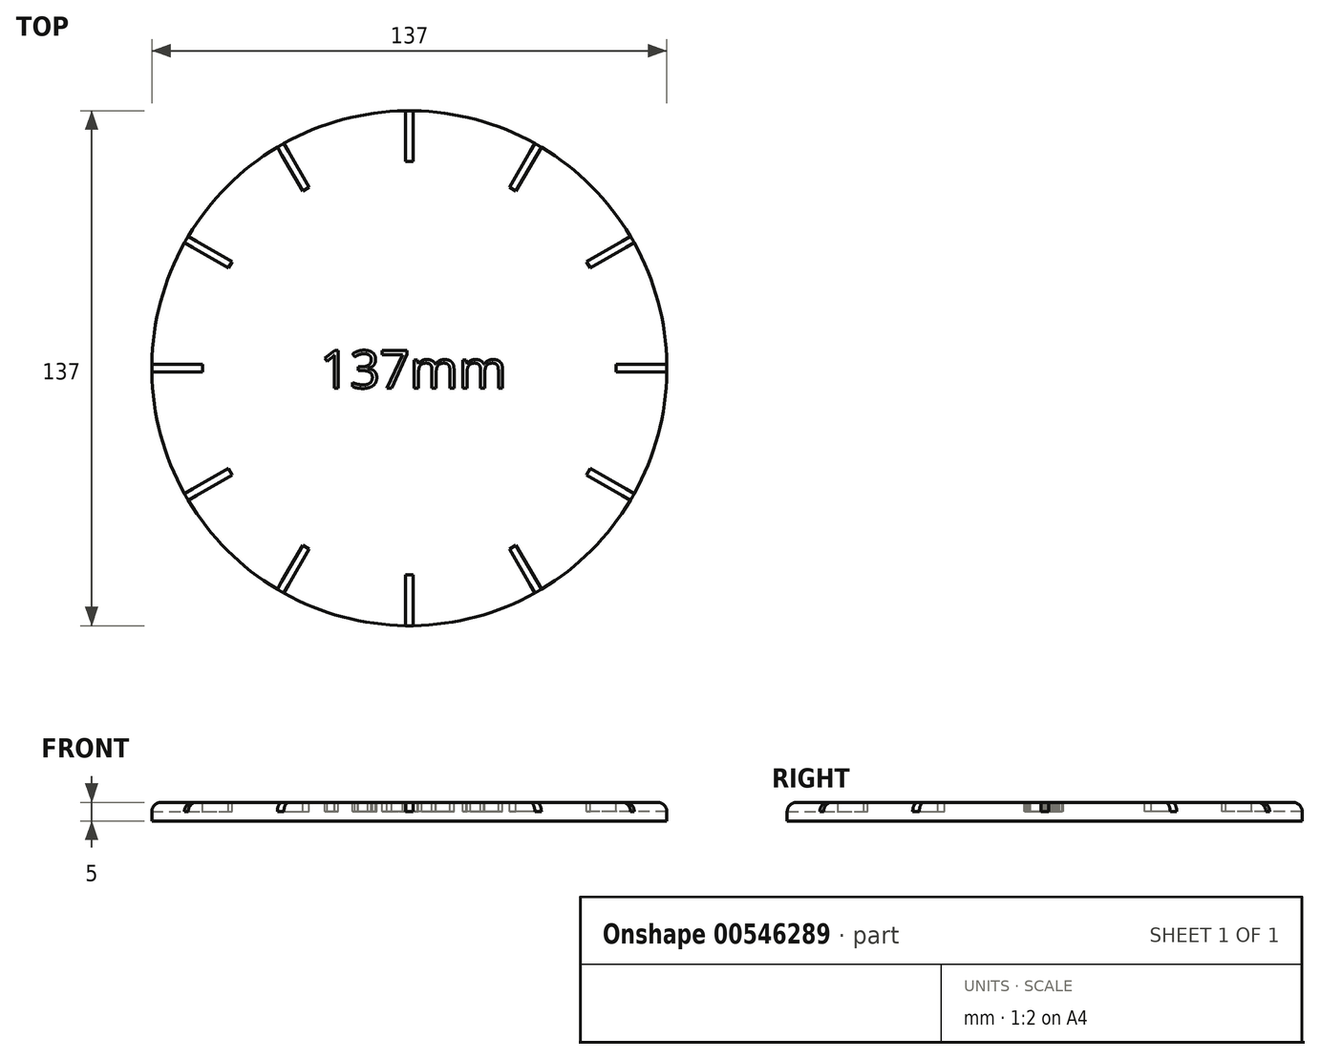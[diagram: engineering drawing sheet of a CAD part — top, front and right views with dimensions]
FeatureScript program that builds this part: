
annotation { "Feature Type Name" : "Feature", "Feature Type Description" : "" }
export const myFeature = defineFeature(function(context is Context, id is Id, definition is map)
    precondition{}
    {
        {
            var Q0;
            Q0=qCreatedBy(makeId("Top.planeOp"),FACE);
            var sketch = newSketch(context, id + "F0", { "sketchPlane" : qUnion([Q0])});
            skCircle(sketch, "E0", {"center": v(0, 0) * mm, "radius": 68.5 * mm});
            skSolve(sketch);
        }
        {
            var Q0;
            Q0=qSketchRegion(id+"F0",true);
            extrude(context, id + "F1", {"entities" : qUnion([Q0]), "depth" : 5 * mm, "offsetDistance" : 25 * mm});
        }
        {
            var Q0;
            Q0=makeQuery(id+"F1.opExtrude","CAP_FACE",FACE,{"disambiguationData":[OSD([sQuery(id+"F0.wireOp",EDGE,"E0")])],"isStart":false});
            var sketch = newSketch(context, id + "F2", { "sketchPlane" : qUnion([Q0])});
            skLineSegment(sketch, "E1.bottom", {"start": v(-1, 70) * mm, "end": v(1, 70) * mm});
            skLineSegment(sketch, "E1.top", {"start": v(-1, 55) * mm, "end": v(1, 55) * mm});
            skLineSegment(sketch, "E1.left", {"start": v(-1, 70) * mm, "end": v(-1, 55) * mm});
            skLineSegment(sketch, "E1.right", {"start": v(1, 70) * mm, "end": v(1, 55) * mm});
            skLineSegment(sketch, "E2.1.0", {"start": v(-35.87, 60.12) * mm, "end": v(-28.37, 47.13) * mm});
            skLineSegment(sketch, "E2.1.1", {"start": v(-34.13, 61.12) * mm, "end": v(-26.63, 48.13) * mm});
            skLineSegment(sketch, "E2.1.2", {"start": v(-28.37, 47.13) * mm, "end": v(-26.63, 48.13) * mm});
            skLineSegment(sketch, "E2.1.3", {"start": v(-35.87, 60.12) * mm, "end": v(-34.13, 61.12) * mm});
            skLineSegment(sketch, "E2.2.0", {"start": v(-61.12, 34.13) * mm, "end": v(-48.13, 26.63) * mm});
            skLineSegment(sketch, "E2.2.1", {"start": v(-60.12, 35.87) * mm, "end": v(-47.13, 28.37) * mm});
            skLineSegment(sketch, "E2.2.2", {"start": v(-48.13, 26.63) * mm, "end": v(-47.13, 28.37) * mm});
            skLineSegment(sketch, "E2.2.3", {"start": v(-61.12, 34.13) * mm, "end": v(-60.12, 35.87) * mm});
            skPoint(sketch, "E2.center", {"position": v(0, 0) * mm});
            skLineSegment(sketch, "E3.2.3.0", {"start": v(-70, -1) * mm, "end": v(-55, -1) * mm});
            skLineSegment(sketch, "E3.3.3.0", {"start": v(-70, 1) * mm, "end": v(-55, 1) * mm});
            skLineSegment(sketch, "E3.6.3.0", {"start": v(-55, -1) * mm, "end": v(-55, 1) * mm});
            skLineSegment(sketch, "E3.9.3.0", {"start": v(-70, -1) * mm, "end": v(-70, 1) * mm});
            skLineSegment(sketch, "E3.2.4.0", {"start": v(-60.12, -35.87) * mm, "end": v(-47.13, -28.37) * mm});
            skLineSegment(sketch, "E3.3.4.0", {"start": v(-61.12, -34.13) * mm, "end": v(-48.13, -26.63) * mm});
            skLineSegment(sketch, "E3.6.4.0", {"start": v(-47.13, -28.37) * mm, "end": v(-48.13, -26.63) * mm});
            skLineSegment(sketch, "E3.9.4.0", {"start": v(-60.12, -35.87) * mm, "end": v(-61.12, -34.13) * mm});
            skLineSegment(sketch, "E3.2.5.0", {"start": v(-34.13, -61.12) * mm, "end": v(-26.63, -48.13) * mm});
            skLineSegment(sketch, "E3.3.5.0", {"start": v(-35.87, -60.12) * mm, "end": v(-28.37, -47.13) * mm});
            skLineSegment(sketch, "E3.6.5.0", {"start": v(-26.63, -48.13) * mm, "end": v(-28.37, -47.13) * mm});
            skLineSegment(sketch, "E3.9.5.0", {"start": v(-34.13, -61.12) * mm, "end": v(-35.87, -60.12) * mm});
            skLineSegment(sketch, "E3.2.6.0", {"start": v(1, -70) * mm, "end": v(1, -55) * mm});
            skLineSegment(sketch, "E3.3.6.0", {"start": v(-1, -70) * mm, "end": v(-1, -55) * mm});
            skLineSegment(sketch, "E3.6.6.0", {"start": v(1, -55) * mm, "end": v(-1, -55) * mm});
            skLineSegment(sketch, "E3.9.6.0", {"start": v(1, -70) * mm, "end": v(-1, -70) * mm});
            skLineSegment(sketch, "E3.2.7.0", {"start": v(35.87, -60.12) * mm, "end": v(28.37, -47.13) * mm});
            skLineSegment(sketch, "E3.3.7.0", {"start": v(34.13, -61.12) * mm, "end": v(26.63, -48.13) * mm});
            skLineSegment(sketch, "E3.6.7.0", {"start": v(28.37, -47.13) * mm, "end": v(26.63, -48.13) * mm});
            skLineSegment(sketch, "E3.9.7.0", {"start": v(35.87, -60.12) * mm, "end": v(34.13, -61.12) * mm});
            skLineSegment(sketch, "E3.2.8.0", {"start": v(61.12, -34.13) * mm, "end": v(48.13, -26.63) * mm});
            skLineSegment(sketch, "E3.3.8.0", {"start": v(60.12, -35.87) * mm, "end": v(47.13, -28.37) * mm});
            skLineSegment(sketch, "E3.6.8.0", {"start": v(48.13, -26.63) * mm, "end": v(47.13, -28.37) * mm});
            skLineSegment(sketch, "E3.9.8.0", {"start": v(61.12, -34.13) * mm, "end": v(60.12, -35.87) * mm});
            skLineSegment(sketch, "E3.2.9.0", {"start": v(70, 1) * mm, "end": v(55, 1) * mm});
            skLineSegment(sketch, "E3.3.9.0", {"start": v(70, -1) * mm, "end": v(55, -1) * mm});
            skLineSegment(sketch, "E3.6.9.0", {"start": v(55, 1) * mm, "end": v(55, -1) * mm});
            skLineSegment(sketch, "E3.9.9.0", {"start": v(70, 1) * mm, "end": v(70, -1) * mm});
            skLineSegment(sketch, "E3.2.10.0", {"start": v(60.12, 35.87) * mm, "end": v(47.13, 28.37) * mm});
            skLineSegment(sketch, "E3.3.10.0", {"start": v(61.12, 34.13) * mm, "end": v(48.13, 26.63) * mm});
            skLineSegment(sketch, "E3.6.10.0", {"start": v(47.13, 28.37) * mm, "end": v(48.13, 26.63) * mm});
            skLineSegment(sketch, "E3.9.10.0", {"start": v(60.12, 35.87) * mm, "end": v(61.12, 34.13) * mm});
            skLineSegment(sketch, "E3.2.11.0", {"start": v(34.13, 61.12) * mm, "end": v(26.63, 48.13) * mm});
            skLineSegment(sketch, "E3.3.11.0", {"start": v(35.87, 60.12) * mm, "end": v(28.37, 47.13) * mm});
            skLineSegment(sketch, "E3.6.11.0", {"start": v(26.63, 48.13) * mm, "end": v(28.37, 47.13) * mm});
            skLineSegment(sketch, "E3.9.11.0", {"start": v(34.13, 61.12) * mm, "end": v(35.87, 60.12) * mm});
            skSolve(sketch);
        }
        {
            var Q0;
            Q0=qSketchRegion(id+"F2",true);
            extrude(context, id + "F3", {"entities" : qUnion([Q0]), "operationType" : NewBodyOperationType.REMOVE, "oppositeDirection" : true, "depth" : 2.5 * mm, "offsetDistance" : 25 * mm});
        }
        {
            var Q0;
            Q0=makeQuery(id+"F1.opExtrude","CAP_FACE",FACE,{"disambiguationData":[OSD([sQuery(id+"F0.wireOp",EDGE,"E0")])],"isStart":false});
            var sketch = newSketch(context, id + "F4", { "sketchPlane" : qUnion([Q0])});
            skText(sketch, "E4", { "text": "137mm\n", "fontName": "OpenSans-Regular.ttf"});
            const initialGuessF4  = {"E4": [-0.02373, -0.00525, 1, 0, 0.01]};
            skSetInitialGuess(sketch, initialGuessF4);
            skSolve(sketch);
        }
        {
            var Q0;
            Q0=qSketchRegion(id+"F4",true);
            extrude(context, id + "F5", {"entities" : qUnion([Q0]), "operationType" : NewBodyOperationType.REMOVE, "oppositeDirection" : true, "depth" : 2.5 * mm, "offsetDistance" : 25 * mm});
        }
        {
            var Q0;
            {var subQ0=sQuery(id+"F0.wireOp",EDGE,"E0");Q0=makeQuery(id+"F3.boolean.opBoolean","SPLIT",EDGE,{"disambiguationData":[TD([makeQuery(id+"F3.opExtrude","SWEPT_FACE",FACE,{"disambiguationData":[OSD([sQuery(id+"F2.wireOp",EDGE,"E3.2.10.0")])]})])],"derivedFrom":makeQuery(id+"F1.opExtrude","CAP_EDGE",EDGE,{"disambiguationData":[OSD([subQ0])],"isStart":false})});}
            var Q1;
            {var subQ0=sQuery(id+"F0.wireOp",EDGE,"E0");Q1=makeQuery(id+"F3.boolean.opBoolean","SPLIT",EDGE,{"disambiguationData":[TD([makeQuery(id+"F3.opExtrude","SWEPT_FACE",FACE,{"disambiguationData":[OSD([sQuery(id+"F2.wireOp",EDGE,"E3.2.9.0")])]})])],"derivedFrom":makeQuery(id+"F1.opExtrude","CAP_EDGE",EDGE,{"disambiguationData":[OSD([subQ0])],"isStart":false})});}
            var Q2;
            {var subQ0=sQuery(id+"F0.wireOp",EDGE,"E0");Q2=makeQuery(id+"F3.boolean.opBoolean","SPLIT",EDGE,{"disambiguationData":[TD([makeQuery(id+"F3.opExtrude","SWEPT_FACE",FACE,{"disambiguationData":[OSD([sQuery(id+"F2.wireOp",EDGE,"E3.2.8.0")])]})])],"derivedFrom":makeQuery(id+"F1.opExtrude","CAP_EDGE",EDGE,{"disambiguationData":[OSD([subQ0])],"isStart":false})});}
            var Q3;
            {var subQ0=sQuery(id+"F0.wireOp",EDGE,"E0");Q3=makeQuery(id+"F3.boolean.opBoolean","SPLIT",EDGE,{"disambiguationData":[TD([makeQuery(id+"F3.opExtrude","SWEPT_FACE",FACE,{"disambiguationData":[OSD([sQuery(id+"F2.wireOp",EDGE,"E3.2.7.0")])]})])],"derivedFrom":makeQuery(id+"F1.opExtrude","CAP_EDGE",EDGE,{"disambiguationData":[OSD([subQ0])],"isStart":false})});}
            var Q4;
            {var subQ0=sQuery(id+"F0.wireOp",EDGE,"E0");Q4=makeQuery(id+"F3.boolean.opBoolean","SPLIT",EDGE,{"disambiguationData":[TD([makeQuery(id+"F3.opExtrude","SWEPT_FACE",FACE,{"disambiguationData":[OSD([sQuery(id+"F2.wireOp",EDGE,"E3.2.6.0")])]})])],"derivedFrom":makeQuery(id+"F1.opExtrude","CAP_EDGE",EDGE,{"disambiguationData":[OSD([subQ0])],"isStart":false})});}
            var Q5;
            {var subQ0=sQuery(id+"F0.wireOp",EDGE,"E0");Q5=makeQuery(id+"F3.boolean.opBoolean","SPLIT",EDGE,{"disambiguationData":[TD([makeQuery(id+"F3.opExtrude","SWEPT_FACE",FACE,{"disambiguationData":[OSD([sQuery(id+"F2.wireOp",EDGE,"E3.2.5.0")])]})])],"derivedFrom":makeQuery(id+"F1.opExtrude","CAP_EDGE",EDGE,{"disambiguationData":[OSD([subQ0])],"isStart":false})});}
            var Q6;
            {var subQ0=sQuery(id+"F0.wireOp",EDGE,"E0");Q6=makeQuery(id+"F3.boolean.opBoolean","SPLIT",EDGE,{"disambiguationData":[TD([makeQuery(id+"F3.opExtrude","SWEPT_FACE",FACE,{"disambiguationData":[OSD([sQuery(id+"F2.wireOp",EDGE,"E3.2.4.0")])]})])],"derivedFrom":makeQuery(id+"F1.opExtrude","CAP_EDGE",EDGE,{"disambiguationData":[OSD([subQ0])],"isStart":false})});}
            var Q7;
            {var subQ0=sQuery(id+"F0.wireOp",EDGE,"E0");Q7=makeQuery(id+"F3.boolean.opBoolean","SPLIT",EDGE,{"disambiguationData":[TD([makeQuery(id+"F3.opExtrude","SWEPT_FACE",FACE,{"disambiguationData":[OSD([sQuery(id+"F2.wireOp",EDGE,"E3.2.3.0")])]})])],"derivedFrom":makeQuery(id+"F1.opExtrude","CAP_EDGE",EDGE,{"disambiguationData":[OSD([subQ0])],"isStart":false})});}
            var Q8;
            {var subQ0=sQuery(id+"F0.wireOp",EDGE,"E0");Q8=makeQuery(id+"F3.boolean.opBoolean","SPLIT",EDGE,{"disambiguationData":[TD([makeQuery(id+"F3.opExtrude","SWEPT_FACE",FACE,{"disambiguationData":[OSD([sQuery(id+"F2.wireOp",EDGE,"E2.2.0")])]})])],"derivedFrom":makeQuery(id+"F1.opExtrude","CAP_EDGE",EDGE,{"disambiguationData":[OSD([subQ0])],"isStart":false})});}
            var Q9;
            {var subQ0=sQuery(id+"F0.wireOp",EDGE,"E0");Q9=makeQuery(id+"F3.boolean.opBoolean","SPLIT",EDGE,{"disambiguationData":[TD([makeQuery(id+"F3.opExtrude","SWEPT_FACE",FACE,{"disambiguationData":[OSD([sQuery(id+"F2.wireOp",EDGE,"E2.1.0")])]})])],"derivedFrom":makeQuery(id+"F1.opExtrude","CAP_EDGE",EDGE,{"disambiguationData":[OSD([subQ0])],"isStart":false})});}
            var Q10;
            {var subQ0=sQuery(id+"F0.wireOp",EDGE,"E0");Q10=makeQuery(id+"F3.boolean.opBoolean","SPLIT",EDGE,{"disambiguationData":[TD([makeQuery(id+"F3.opExtrude","SWEPT_FACE",FACE,{"disambiguationData":[OSD([sQuery(id+"F2.wireOp",EDGE,"E1.left")])]})])],"derivedFrom":makeQuery(id+"F1.opExtrude","CAP_EDGE",EDGE,{"disambiguationData":[OSD([subQ0])],"isStart":false})});}
            var Q11;
            {var subQ0=sQuery(id+"F0.wireOp",EDGE,"E0");Q11=makeQuery(id+"F3.boolean.opBoolean","SPLIT",EDGE,{"disambiguationData":[TD([makeQuery(id+"F3.opExtrude","SWEPT_FACE",FACE,{"disambiguationData":[OSD([sQuery(id+"F2.wireOp",EDGE,"E1.right")])]})])],"derivedFrom":makeQuery(id+"F1.opExtrude","CAP_EDGE",EDGE,{"disambiguationData":[OSD([subQ0])],"isStart":false})});}
            fillet(context, id + "F6", {"entities" : qUnion([Q0, Q1, Q2, Q3, Q4, Q5, Q6, Q7, Q8, Q9, Q10, Q11]), "radius" : 2.5 * mm, "tangentPropagation" : true, "allowEdgeOverflow" : false});
        }
    });
